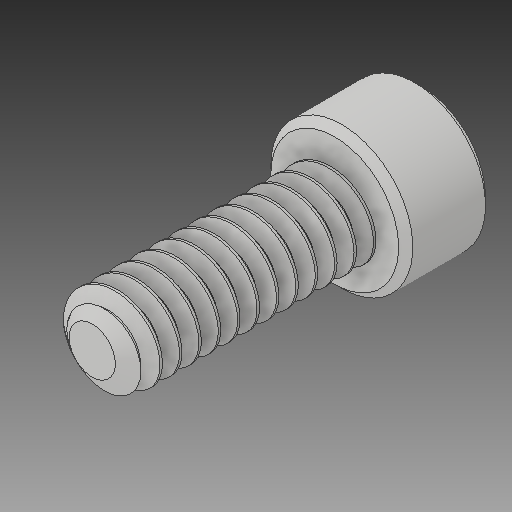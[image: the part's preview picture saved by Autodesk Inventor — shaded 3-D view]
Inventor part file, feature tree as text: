
AUTODESK INVENTOR PART (.ipt)
format: ipt  version: 2017 (Build 210142000, 142)  size: 635,904 bytes
history: native  units: in
note: dims shown in document units (in); Inventor stores cm internally (conversion verified against a paired STEP export)
features: chamfer x1
ambient origin geometry x8: Origin, YZ Plane, XZ Plane, XY Plane, X Axis, Y Axis, Z Axis, Center Point
bodies: Solid1 (feature_tree)
feature tree (1):
  chamfer  "Chamfer1"  [1 undecoded]
note: 1 required parameter value undecoded (feature->parameter linkage not recoverable at this tier; creation-order binding heuristic only, values carry confidence <= 0.55)
